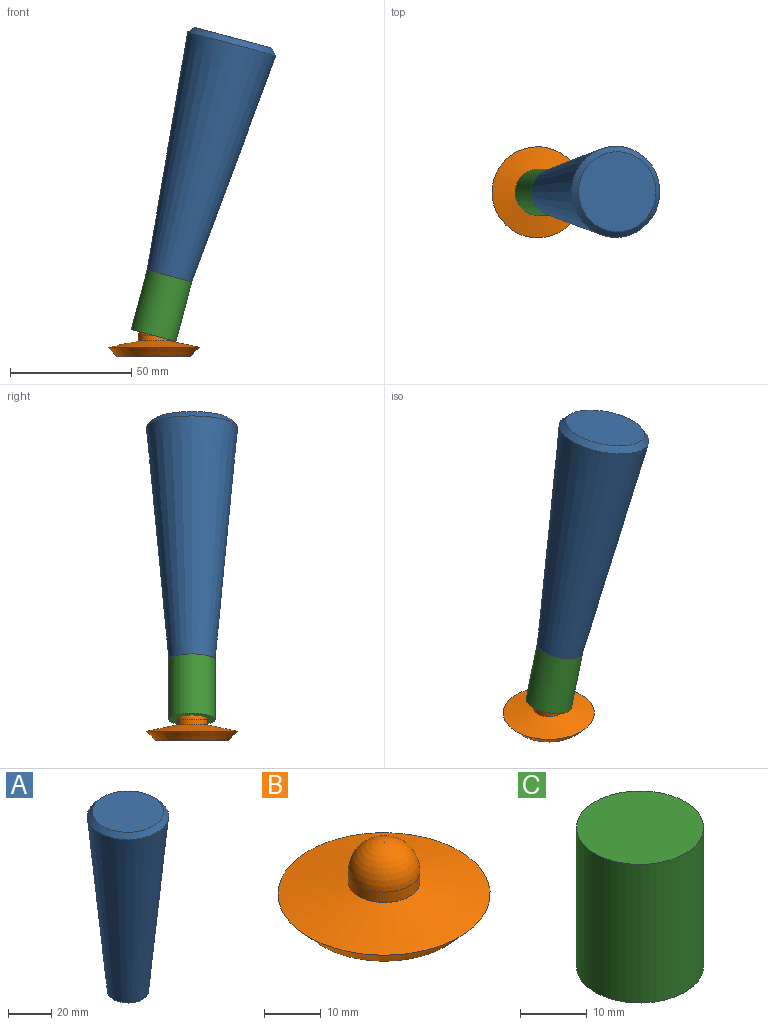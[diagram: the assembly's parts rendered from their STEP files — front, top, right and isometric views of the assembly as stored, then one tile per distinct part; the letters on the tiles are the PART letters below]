
ASSEMBLY  parts=3 mates=2
PART A: 4 faces, bbox 37.6x37.6x101.6 mm
  f0: plane 19.05x19.05mm, normal (0,0,-1), area 285mm2, adj f1
  f1: cone r=9.53mm half-angle=5.4deg, axis (0,0,1), area 8858.6mm2, adj f0,f3
  f2: plane 33.02x33.02mm, normal (0,0,1), area 856.3mm2, adj f3
  f3: cone r=16.51mm half-angle=42.3deg, axis (0,0,-1), area 379.6mm2, adj f1,f2
PART B: 5 faces, bbox 37.5x37.5x15 mm
  f0: plane 30.48x30.48mm, normal (0,0,-1), area 729.7mm2, adj f1
  f1: cone r=15.24mm half-angle=43deg, axis (0,0,1), area 553.9mm2, adj f0,f2
  f2: cone r=18.77mm half-angle=78deg, axis (0,0,-1), area 1002.4mm2, adj f1,f3
  f3: cylinder r=6.35mm len=12.7mm, axis (0,0,1), area 90.5mm2, adj f2,f4
  f4: sphere r=6.35mm, area 253.4mm2, adj f3
PART C: 3 faces, bbox 19.1x19.1x25.4 mm
  f0: cylinder r=9.53mm len=25.4mm, axis (0,0,-1), area 1520.1mm2, adj f1,f2
  f1: plane 19.05x19.05mm, normal (0,0,1), area 285mm2, adj f0
  f2: plane 19.05x19.05mm, normal (0,0,-1), area 285mm2, adj f0
PLACE A rot(axis=(0,1,0),15deg) t=(-6.61,-0.58,-32.83)mm
PLACE B t=(0.47,-0.58,-15.1)mm fixed
PLACE C rot(axis=(-0.13,0,-0.99),180deg) t=(0.47,-0.58,-6.4)mm
MATE fastened A.f1 <-> C.f0  axis (-0.26,0,-0.97) through (7.05,-0.58,18.13)mm
MATE ball C.f0 <-> B.f1  axis (-0.26,0,-0.97) through (0.47,-0.58,-6.4)mm
